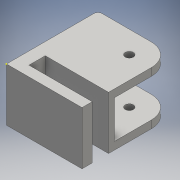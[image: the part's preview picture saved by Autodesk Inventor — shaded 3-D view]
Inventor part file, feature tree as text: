
AUTODESK INVENTOR PART (.ipt)
format: ipt  version: 2016 (Build 200138000, 138)  size: 141,312 bytes
history: native  units: mm
features: sketch x5, extrude x4, fillet x2
ambient origin geometry x8: Origin, YZ Plane, XZ Plane, XY Plane, X Axis, Y Axis, Z Axis, Center Point
bodies: Solid1 (feature_tree)
feature tree (11):
  extrude  "Extrusion1"  Depth=8.0mm
  sketch  "Sketch2"  dims[d7=20.0mm d8=4.0mm]
  extrude  "Extrusion2"  Depth=4.0mm
  extrude  "Extrusion3"  Depth=5.0mm
  extrude  "Extrusion4"  Depth=37.004321mm
  fillet  "Fillet1"  Radius=31.004321mm
  fillet  "Fillet2"  Radius=26.0mm
  sketch  "Sketch1"  dims[d3=8.0mm d6=18.0mm]
  sketch  "Sketch3"  dims[d9=3.0mm d10=5.0mm]
  sketch  "Sketch4"  dims[d11=16.0mm d12=37.004321mm d13=31.004321mm d15=26.0mm d16=0.0mm]
  sketch  "Sketch5"  dims[d19=9.25mm d20=9.25mm d21=26.0mm d22=0.0mm d23=26.0mm d24=0.0mm d25=26.0mm d26=0.0mm d27=2.0mm d28=2.0mm]
